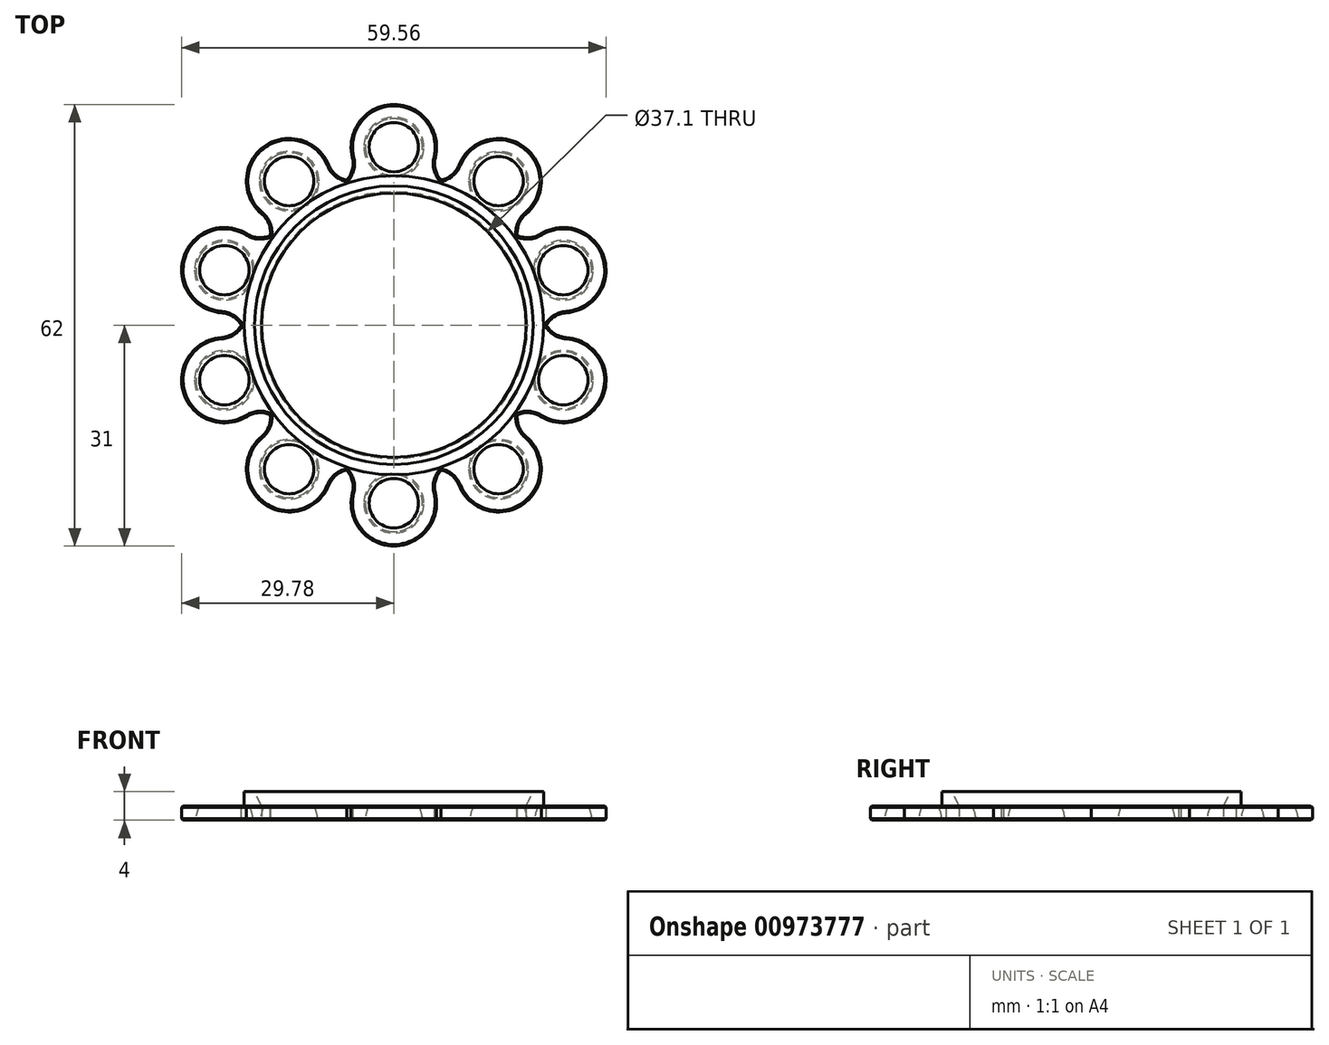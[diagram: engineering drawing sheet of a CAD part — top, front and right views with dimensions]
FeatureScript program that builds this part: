
annotation { "Feature Type Name" : "Feature", "Feature Type Description" : "" }
export const myFeature = defineFeature(function(context is Context, id is Id, definition is map)
    precondition{}
    {
        {
            var Q0;
            Q0=qCreatedBy(makeId("Top.planeOp"),FACE);
            var sketch = newSketch(context, id + "F0", { "sketchPlane" : qUnion([Q0])});
            skCircle(sketch, "E0", {"center": v(0, 0) * mm, "radius": 18.55 * mm});
            skArc(sketch, "E1", {"start": v(-4.08, 20.6) * mm, "mid": v(0, -21) * mm, "end": v(4.08, 20.6) * mm});
            skCircle(sketch, "E2", {"center": v(0, 25) * mm, "radius": 1.5 * mm});
            skArc(sketch, "E3", {"start": v(4.08, 20.6) * mm, "mid": v(0, 31) * mm, "end": v(-4.08, 20.6) * mm});
            skSolve(sketch);
        }
        {
            var Q0;
            {var subQ0=sQuery(id+"F0.wireOp",EDGE,"E0");Q0=makeQuery(id+"F0.imprint","IMPRINT",FACE,{"disambiguationData":[TD([[makeQuery(id+"F0.imprint","IMPRINT",EDGE,{"derivedFrom":subQ0}),-1.0]])]});}
            var Q1;
            {var subQ0=sQuery(id+"F0.wireOp",EDGE,"E3");var subQ1=sQuery(id+"F0.wireOp",EDGE,"E1");var subQ2=makeQuery(id+"F0.imprint","INTERSECT",VERTEX,{"disambiguationData":[OD(0.0)],"derivedFrom":[subQ1,subQ0]});Q1=makeQuery(id+"F0.imprint","IMPRINT",FACE,{"disambiguationData":[TD([[makeQuery(id+"F0.imprint","IMPRINT",EDGE,{"disambiguationData":[TD([[subQ2,1.0]])],"derivedFrom":subQ1}),1.0]])]});}
            extrude(context, id + "F1", {"entities" : qUnion([Q0, Q1]), "depth" : 4 * mm, "offsetDistance" : 25 * mm});
        }
        {
            var Q0;
            Q0=makeQuery(id+"F0.imprint","IMPRINT",FACE,{"disambiguationData":[TD([[makeQuery(id+"F0.imprint","IMPRINT",EDGE,{"derivedFrom":sQuery(id+"F0.wireOp",EDGE,"E2")}),-1.0]])]});
            extrude(context, id + "F2", {"entities" : qUnion([Q0]), "operationType" : NewBodyOperationType.ADD, "depth" : 2 * mm, "offsetDistance" : 25 * mm});
        }
        {
            var Q0;
            Q0=makeQuery(id+"F0.imprint","IMPRINT",FACE,{"disambiguationData":[TD([[makeQuery(id+"F0.imprint","IMPRINT",EDGE,{"derivedFrom":sQuery(id+"F0.wireOp",EDGE,"E2")}),-1.0]])]});
            var sketch = newSketch(context, id + "F3", { "sketchPlane" : qUnion([Q0])});
            skArc(sketch, "E4", {"start": v(0, 29) * mm, "mid": v(-4, 25) * mm, "end": v(0, 21) * mm});
            skLineSegment(sketch, "E5", {"start": v(0, 29) * mm, "end": v(0, 21) * mm});
            skSolve(sketch);
        }
        {
            var Q0;
            Q0 = qSketchRegion(id + "F3", true);
            var Q1;
            {var subQ0=sQuery(id+"F3.wireOp",EDGE,"E4");var subQ5=sQuery(id+"F3.wireOp",EDGE,"E5");var subQ9=makeQuery(id+"F3.imprint","INTERSECT",VERTEX,{"disambiguationData":[OD(0.0)],"derivedFrom":[subQ0,subQ5]});Q1=makeQuery(id+"F3.imprint","IMPRINT",FACE,{"disambiguationData":[TD([[makeQuery(id+"F3.imprint","IMPRINT",EDGE,{"disambiguationData":[TD([[subQ9,-1.0]])],"derivedFrom":subQ5}),-1.0]])]});}
            var Q2;
            Q2=sQuery(id+"F3.wireOp",EDGE,"E5");
            revolve(context, id + "F4", {"operationType" : NewBodyOperationType.REMOVE, "surfaceOperationType" : NewSurfaceOperationType.NEW, "entities" : qUnion([Q0, Q1]), "axis" : qUnion([Q2]), "revolveType" : RevolveType.FULL, "oppositeDirection" : true});
        }
        {
            var Q0;
            Q0=makeQuery(id+"F1.opExtrude","CAP_FACE",FACE,{"disambiguationData":[OSD([sQuery(id+"F0.wireOp",EDGE,"E0"),sQuery(id+"F0.wireOp",EDGE,"E1"),sQuery(id+"F0.wireOp",EDGE,"E2"),sQuery(id+"F0.wireOp",EDGE,"E3")])],"isStart":false});
            var sketch = newSketch(context, id + "F5", { "sketchPlane" : qUnion([Q0])});
            skCircle(sketch, "E6", {"center": v(0, 25) * mm, "radius": 6 * mm});
            skCircle(sketch, "E7", {"center": v(0, 0) * mm, "radius": 21 * mm});
            skSolve(sketch);
        }
        {
            var Q0;
            Q0=makeQuery(id+"F5.imprint","IMPRINT",FACE,{"disambiguationData":[TD([[makeQuery(id+"F5.imprint","IMPRINT",EDGE,{"derivedFrom":makeQuery(id+"F1.opExtrude","CAP_EDGE",EDGE,{"disambiguationData":[OSD([sQuery(id+"F0.wireOp",EDGE,"E2")])],"isStart":false})}),-1.0]])]});
            extrude(context, id + "F6", {"entities" : qUnion([Q0]), "operationType" : NewBodyOperationType.REMOVE, "oppositeDirection" : true, "depth" : 2 * mm, "offsetDistance" : 25 * mm});
        }
        {
            var Q0;
            {var subQ0=sQuery(id+"F0.wireOp",EDGE,"E3");var subQ1=sQuery(id+"F0.wireOp",EDGE,"E1");Q0=makeQuery(id+"F1.opExtrude","SWEPT_EDGE",EDGE,{"disambiguationData":[OSD([subQ1,subQ0]),TDD([makeQuery(id+"F0.imprint","INTERSECT",VERTEX,{"disambiguationData":[OD(1.0)],"derivedFrom":[subQ1,subQ0]})])]});}
            var Q1;
            {var subQ0=sQuery(id+"F0.wireOp",EDGE,"E3");var subQ1=sQuery(id+"F0.wireOp",EDGE,"E1");Q1=makeQuery(id+"F1.opExtrude","SWEPT_EDGE",EDGE,{"disambiguationData":[OSD([subQ1,subQ0]),TDD([makeQuery(id+"F0.imprint","INTERSECT",VERTEX,{"disambiguationData":[OD(0.0)],"derivedFrom":[subQ1,subQ0]})])]});}
            fillet(context, id + "F7", {"entities" : qUnion([Q0, Q1]), "radius" : 3.5 * mm, "tangentPropagation" : true, "allowEdgeOverflow" : false});
        }
        {
            var Q0;
            Q0=makeQuery(id+"F6.boolean.opBoolean","COPY",EDGE,{"derivedFrom":makeQuery(id+"F6.opExtrude","CAP_EDGE",EDGE,{"disambiguationData":[OSD([sQuery(id+"F5.wireOp",EDGE,"E6")])],"isStart":false})});
            var Q1;
            {var subQ0=sQuery(id+"F0.wireOp",EDGE,"E3");var subQ1=sQuery(id+"F0.wireOp",EDGE,"E1");Q1=makeQuery(id+"F7.opFillet","BLEND_EDGE",EDGE,{"blendedFrom":[makeQuery(id+"F1.opExtrude","SWEPT_EDGE",EDGE,{"disambiguationData":[OSD([subQ1,subQ0]),TDD([makeQuery(id+"F0.imprint","INTERSECT",VERTEX,{"disambiguationData":[OD(0.0)],"derivedFrom":[subQ1,subQ0]})])]}),makeQuery(id+"F6.boolean.opBoolean","COPY",FACE,{"derivedFrom":makeQuery(id+"F6.opExtrude","CAP_FACE",FACE,{"disambiguationData":[OSD([sQuery(id+"F0.wireOp",EDGE,"E2"),sQuery(id+"F5.wireOp",EDGE,"E6"),sQuery(id+"F5.wireOp",EDGE,"E7")])],"isStart":false})})],"blendedInto":[makeQuery(id+"F6.boolean.opBoolean","COPY",FACE,{"derivedFrom":makeQuery(id+"F6.opExtrude","CAP_FACE",FACE,{"disambiguationData":[OSD([sQuery(id+"F0.wireOp",EDGE,"E2"),sQuery(id+"F5.wireOp",EDGE,"E6"),sQuery(id+"F5.wireOp",EDGE,"E7")])],"isStart":false})})]});}
            var Q2;
            {var subQ0=sQuery(id+"F0.wireOp",EDGE,"E3");var subQ1=sQuery(id+"F0.wireOp",EDGE,"E1");Q2=makeQuery(id+"F7.opFillet","BLEND_EDGE",EDGE,{"blendedFrom":[makeQuery(id+"F1.opExtrude","SWEPT_EDGE",EDGE,{"disambiguationData":[OSD([subQ1,subQ0]),TDD([makeQuery(id+"F0.imprint","INTERSECT",VERTEX,{"disambiguationData":[OD(1.0)],"derivedFrom":[subQ1,subQ0]})])]}),makeQuery(id+"F6.boolean.opBoolean","COPY",FACE,{"derivedFrom":makeQuery(id+"F6.opExtrude","CAP_FACE",FACE,{"disambiguationData":[OSD([sQuery(id+"F0.wireOp",EDGE,"E2"),sQuery(id+"F5.wireOp",EDGE,"E6"),sQuery(id+"F5.wireOp",EDGE,"E7")])],"isStart":false})})],"blendedInto":[makeQuery(id+"F6.boolean.opBoolean","COPY",FACE,{"derivedFrom":makeQuery(id+"F6.opExtrude","CAP_FACE",FACE,{"disambiguationData":[OSD([sQuery(id+"F0.wireOp",EDGE,"E2"),sQuery(id+"F5.wireOp",EDGE,"E6"),sQuery(id+"F5.wireOp",EDGE,"E7")])],"isStart":false})})]});}
            chamfer(context, id + "F8", {"entities" : qUnion([Q0, Q1, Q2]), "width" : 0.2 * mm, "tangentPropagation" : true});
        }
        {
            var Q0;
            Q0=makeQuery(id+"F1.opExtrude","SWEPT_BODY",BODY,{"disambiguationData":[OSD([sQuery(id+"F0.wireOp",EDGE,"E0"),sQuery(id+"F0.wireOp",EDGE,"E1"),sQuery(id+"F0.wireOp",EDGE,"E2"),sQuery(id+"F0.wireOp",EDGE,"E3")])]});
            var Q1;
            Q1=sQuery(id+"F0.wireOp",EDGE,"E0");
            circularPattern(context, id + "F9", {"operationType" : NewBodyOperationType.ADD, "entities" : qUnion([Q0]), "axis" : qUnion([Q1]), "angle" : 360 * degree, "instanceCount" : 10, "oppositeDirection" : true, "equalSpace" : true});
        }
        {
            var Q0;
            Q0=makeQuery(id+"F1.opExtrude","CAP_EDGE",EDGE,{"disambiguationData":[OSD([sQuery(id+"F0.wireOp",EDGE,"E0")])],"isStart":false});
            chamfer(context, id + "F10", {"entities" : qUnion([Q0]), "chamferType" : ChamferType.TWO_OFFSETS, "width1" : 2 * mm, "oppositeDirection" : false, "width2" : 1 * mm, "tangentPropagation" : true});
        }
        {
            var Q0;
            {var subQ0=makeQuery(id+"F1.opExtrude","CAP_FACE",FACE,{"disambiguationData":[OSD([sQuery(id+"F0.wireOp",EDGE,"E0"),sQuery(id+"F0.wireOp",EDGE,"E1"),sQuery(id+"F0.wireOp",EDGE,"E2"),sQuery(id+"F0.wireOp",EDGE,"E3")])],"isStart":true});Q0=makeQuery(id+"F9.boolean.opBoolean","MERGE",FACE,{"derivedFrom":[subQ0,makeQuery(id+"F9.opPattern","COPY",FACE,{"derivedFrom":subQ0,"instanceName":"1"}),makeQuery(id+"F9.opPattern","COPY",FACE,{"derivedFrom":subQ0,"instanceName":"2"}),makeQuery(id+"F9.opPattern","COPY",FACE,{"derivedFrom":subQ0,"instanceName":"3"}),makeQuery(id+"F9.opPattern","COPY",FACE,{"derivedFrom":subQ0,"instanceName":"4"}),makeQuery(id+"F9.opPattern","COPY",FACE,{"derivedFrom":subQ0,"instanceName":"5"}),makeQuery(id+"F9.opPattern","COPY",FACE,{"derivedFrom":subQ0,"instanceName":"6"}),makeQuery(id+"F9.opPattern","COPY",FACE,{"derivedFrom":subQ0,"instanceName":"7"}),makeQuery(id+"F9.opPattern","COPY",FACE,{"derivedFrom":subQ0,"instanceName":"8"}),makeQuery(id+"F9.opPattern","COPY",FACE,{"derivedFrom":subQ0,"instanceName":"9"})]});}
            var Q1;
            Q1=makeQuery(id+"F6.boolean.opBoolean","MERGE",EDGE,{"derivedFrom":[makeQuery(id+"F1.opExtrude","CAP_EDGE",EDGE,{"disambiguationData":[OSD([sQuery(id+"F0.wireOp",EDGE,"E1")])],"isStart":false})],"fromTools":[makeQuery(id+"F6.opExtrude","CAP_EDGE",EDGE,{"disambiguationData":[OSD([sQuery(id+"F5.wireOp",EDGE,"E7")])],"isStart":true})]});
            chamfer(context, id + "F11", {"entities" : qUnion([Q0, Q1]), "width" : 0.2 * mm, "tangentPropagation" : true});
        }
    });
